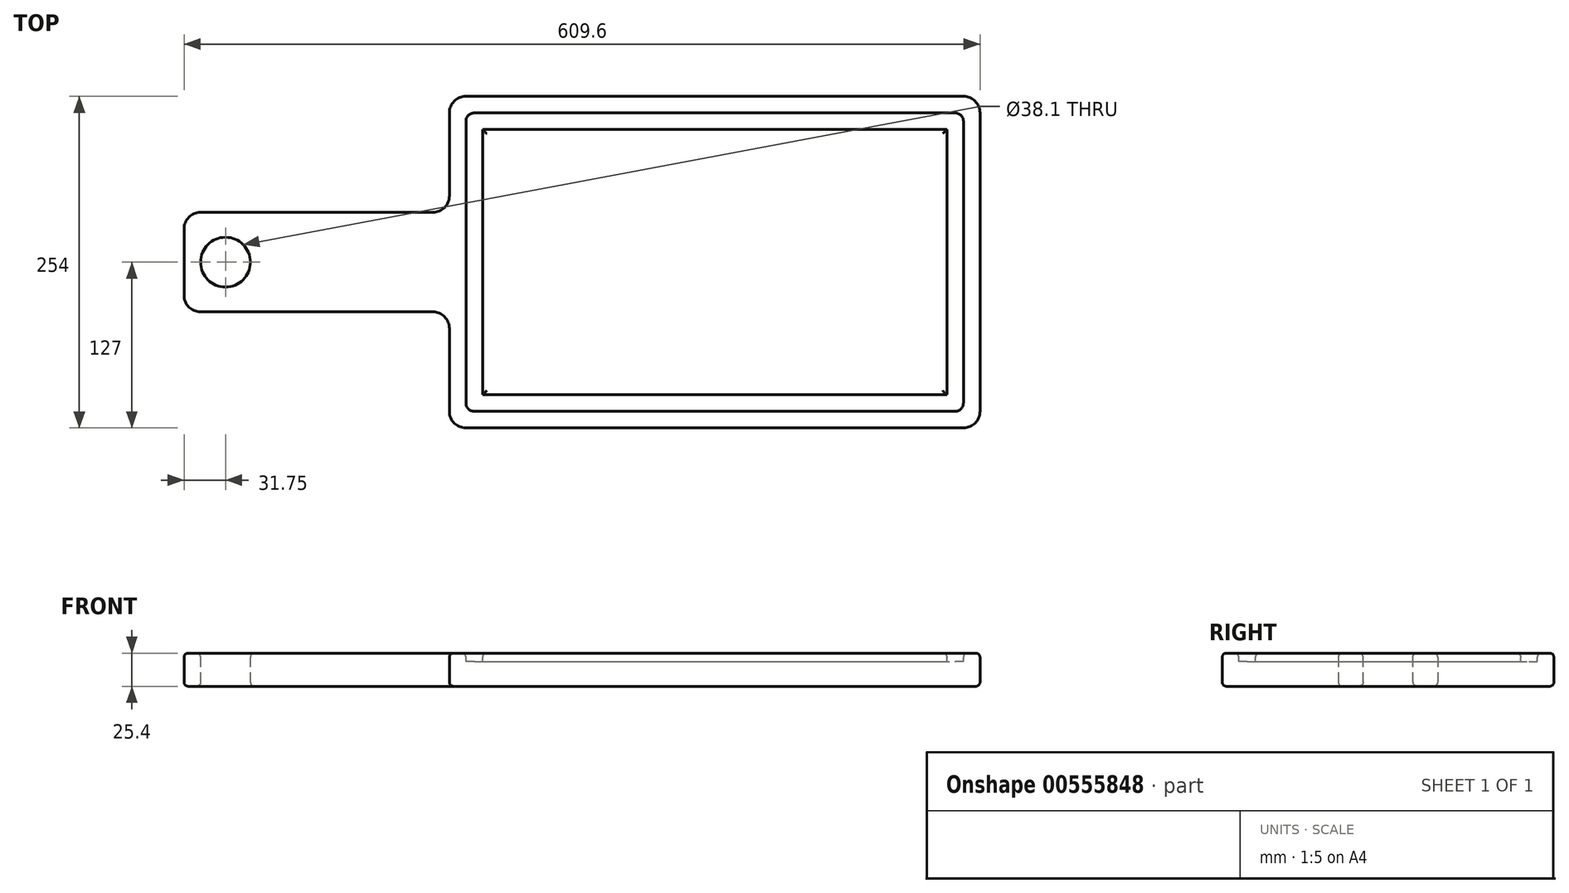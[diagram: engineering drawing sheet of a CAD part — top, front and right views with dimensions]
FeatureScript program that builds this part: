
annotation { "Feature Type Name" : "Feature", "Feature Type Description" : "" }
export const myFeature = defineFeature(function(context is Context, id is Id, definition is map)
    precondition{}
    {
        {
            var Q0;
            Q0=qCreatedBy(makeId("Top.planeOp"),FACE);
            var sketch = newSketch(context, id + "F0", { "sketchPlane" : qUnion([Q0])});
            skLineSegment(sketch, "E0.bottom", {"start": v(0, 0) * mm, "end": v(406.4, 0) * mm});
            skLineSegment(sketch, "E0.top", {"start": v(0, 254) * mm, "end": v(406.4, 254) * mm});
            skLineSegment(sketch, "E0.left", {"start": v(0, 0) * mm, "end": v(0, 254) * mm});
            skLineSegment(sketch, "E0.right", {"start": v(406.4, 0) * mm, "end": v(406.4, 254) * mm});
            skLineSegment(sketch, "E1.bottom", {"start": v(0, 165.1) * mm, "end": v(-203.2, 165.1) * mm});
            skLineSegment(sketch, "E1.top", {"start": v(0, 88.9) * mm, "end": v(-203.2, 88.9) * mm});
            skLineSegment(sketch, "E1.left", {"start": v(0, 165.1) * mm, "end": v(0, 88.9) * mm});
            skLineSegment(sketch, "E1.right", {"start": v(-203.2, 165.1) * mm, "end": v(-203.2, 88.9) * mm});
            skSolve(sketch);
        }
        {
            var Q0;
            {var subQ3=sQuery(id+"F0.wireOp",EDGE,"E0.bottom");Q0=makeQuery(id+"F0.imprint","IMPRINT",FACE,{"disambiguationData":[TD([[makeQuery(id+"F0.imprint","IMPRINT",EDGE,{"derivedFrom":subQ3}),1.0]])]});}
            var Q1;
            Q1=makeQuery(id+"F0.imprint","IMPRINT",FACE,{"disambiguationData":[TD([[makeQuery(id+"F0.imprint","IMPRINT",EDGE,{"derivedFrom":sQuery(id+"F0.wireOp",EDGE,"E1.bottom")}),1.0]])]});
            extrude(context, id + "F1", {"entities" : qUnion([Q0, Q1]), "depth" : 25.4 * mm, "offsetDistance" : 25.4 * mm});
        }
        {
            var Q0;
            Q0=makeQuery(id+"F1.opExtrude","CAP_FACE",FACE,{"disambiguationData":[OSD([sQuery(id+"F0.wireOp",EDGE,"E0.bottom"),sQuery(id+"F0.wireOp",EDGE,"E0.top"),sQuery(id+"F0.wireOp",EDGE,"E0.left"),sQuery(id+"F0.wireOp",EDGE,"E0.right"),sQuery(id+"F0.wireOp",EDGE,"E1.bottom"),sQuery(id+"F0.wireOp",EDGE,"E1.top"),sQuery(id+"F0.wireOp",EDGE,"E1.right")])],"isStart":false});
            var sketch = newSketch(context, id + "F2", { "sketchPlane" : qUnion([Q0])});
            skCircle(sketch, "E2", {"center": v(-171.45, 127) * mm, "radius": 19.05 * mm});
            skSolve(sketch);
        }
        {
            var Q0;
            Q0 = qSketchRegion(id + "F2", true);
            extrude(context, id + "F3", {"entities" : qUnion([Q0]), "operationType" : NewBodyOperationType.REMOVE, "oppositeDirection" : true, "depth" : 25.4 * mm, "offsetDistance" : 25.4 * mm});
        }
        {
            var Q0;
            Q0=makeQuery(id+"F1.opExtrude","CAP_FACE",FACE,{"disambiguationData":[OSD([sQuery(id+"F0.wireOp",EDGE,"E0.bottom"),sQuery(id+"F0.wireOp",EDGE,"E0.top"),sQuery(id+"F0.wireOp",EDGE,"E0.left"),sQuery(id+"F0.wireOp",EDGE,"E0.right"),sQuery(id+"F0.wireOp",EDGE,"E1.bottom"),sQuery(id+"F0.wireOp",EDGE,"E1.top"),sQuery(id+"F0.wireOp",EDGE,"E1.right")])],"isStart":false});
            var sketch = newSketch(context, id + "F4", { "sketchPlane" : qUnion([Q0])});
            skLineSegment(sketch, "E3.0", {"start": v(12.7, 12.7) * mm, "end": v(12.7, 88.9) * mm});
            skLineSegment(sketch, "E3.1", {"start": v(12.7, 165.1) * mm, "end": v(12.7, 241.3) * mm});
            skLineSegment(sketch, "E3.2", {"start": v(12.7, 241.3) * mm, "end": v(393.7, 241.3) * mm});
            skLineSegment(sketch, "E3.3", {"start": v(393.7, 12.7) * mm, "end": v(393.7, 241.3) * mm});
            skLineSegment(sketch, "E3.4", {"start": v(12.7, 12.7) * mm, "end": v(393.7, 12.7) * mm});
            skLineSegment(sketch, "E4", {"start": v(12.7, 165.1) * mm, "end": v(12.7, 88.9) * mm});
            skLineSegment(sketch, "E5.0", {"start": v(25.4, 165.1) * mm, "end": v(25.4, 228.6) * mm});
            skLineSegment(sketch, "E5.1", {"start": v(381, 25.4) * mm, "end": v(381, 228.6) * mm});
            skLineSegment(sketch, "E5.2", {"start": v(25.4, 25.4) * mm, "end": v(381, 25.4) * mm});
            skLineSegment(sketch, "E5.3", {"start": v(25.4, 228.6) * mm, "end": v(381, 228.6) * mm});
            skLineSegment(sketch, "E5.4", {"start": v(25.4, 25.4) * mm, "end": v(25.4, 88.9) * mm});
            skLineSegment(sketch, "E5.5", {"start": v(25.4, 165.1) * mm, "end": v(25.4, 88.9) * mm});
            skSolve(sketch);
        }
        {
            var Q0;
            Q0=makeQuery(id+"F4.imprint","IMPRINT",FACE,{"disambiguationData":[TD([[makeQuery(id+"F4.imprint","IMPRINT",EDGE,{"derivedFrom":sQuery(id+"F4.wireOp",EDGE,"E3.0")}),-1.0]])]});
            extrude(context, id + "F5", {"entities" : qUnion([Q0]), "operationType" : NewBodyOperationType.REMOVE, "oppositeDirection" : true, "depth" : 6.35 * mm, "offsetDistance" : 25.4 * mm});
        }
        {
            var Q0;
            Q0=makeQuery(id+"F5.boolean.opBoolean","COPY",EDGE,{"derivedFrom":makeQuery(id+"F5.opExtrude","SWEPT_EDGE",EDGE,{"disambiguationData":[OSD([sQuery(id+"F4.wireOp",EDGE,"E3.1"),sQuery(id+"F4.wireOp",EDGE,"E3.2")])]})});
            var Q1;
            Q1=makeQuery(id+"F5.boolean.opBoolean","COPY",EDGE,{"derivedFrom":makeQuery(id+"F5.opExtrude","SWEPT_EDGE",EDGE,{"disambiguationData":[OSD([sQuery(id+"F4.wireOp",EDGE,"E3.3"),sQuery(id+"F4.wireOp",EDGE,"E3.4")])]})});
            var Q2;
            Q2=makeQuery(id+"F5.boolean.opBoolean","COPY",EDGE,{"derivedFrom":makeQuery(id+"F5.opExtrude","SWEPT_EDGE",EDGE,{"disambiguationData":[OSD([sQuery(id+"F4.wireOp",EDGE,"E3.0"),sQuery(id+"F4.wireOp",EDGE,"E3.4")])]})});
            var Q3;
            Q3=makeQuery(id+"F5.boolean.opBoolean","COPY",EDGE,{"derivedFrom":makeQuery(id+"F5.opExtrude","SWEPT_EDGE",EDGE,{"disambiguationData":[OSD([sQuery(id+"F4.wireOp",EDGE,"E3.2"),sQuery(id+"F4.wireOp",EDGE,"E3.3")])]})});
            fillet(context, id + "F6", {"entities" : qUnion([Q0, Q1, Q2, Q3]), "radius" : 6.35 * mm, "tangentPropagation" : true, "allowEdgeOverflow" : false});
        }
        {
            var Q0;
            Q0=makeQuery(id+"F1.opExtrude","SWEPT_EDGE",EDGE,{"disambiguationData":[OSD([sQuery(id+"F0.wireOp",EDGE,"E0.bottom"),sQuery(id+"F0.wireOp",EDGE,"E0.right")])]});
            var Q1;
            Q1=makeQuery(id+"F1.opExtrude","SWEPT_EDGE",EDGE,{"disambiguationData":[OSD([sQuery(id+"F0.wireOp",EDGE,"E0.bottom"),sQuery(id+"F0.wireOp",EDGE,"E0.left")])]});
            var Q2;
            Q2=makeQuery(id+"F1.opExtrude","SWEPT_EDGE",EDGE,{"disambiguationData":[OSD([sQuery(id+"F0.wireOp",EDGE,"E0.left"),sQuery(id+"F0.wireOp",EDGE,"E1.top"),sQuery(id+"F0.wireOp",EDGE,"E1.left")])]});
            var Q3;
            Q3=makeQuery(id+"F1.opExtrude","SWEPT_EDGE",EDGE,{"disambiguationData":[OSD([sQuery(id+"F0.wireOp",EDGE,"E1.top"),sQuery(id+"F0.wireOp",EDGE,"E1.right")])]});
            var Q4;
            Q4=makeQuery(id+"F1.opExtrude","SWEPT_EDGE",EDGE,{"disambiguationData":[OSD([sQuery(id+"F0.wireOp",EDGE,"E1.bottom"),sQuery(id+"F0.wireOp",EDGE,"E1.right")])]});
            var Q5;
            Q5=makeQuery(id+"F1.opExtrude","SWEPT_EDGE",EDGE,{"disambiguationData":[OSD([sQuery(id+"F0.wireOp",EDGE,"E0.left"),sQuery(id+"F0.wireOp",EDGE,"E1.bottom"),sQuery(id+"F0.wireOp",EDGE,"E1.left")])]});
            var Q6;
            Q6=makeQuery(id+"F1.opExtrude","SWEPT_EDGE",EDGE,{"disambiguationData":[OSD([sQuery(id+"F0.wireOp",EDGE,"E0.top"),sQuery(id+"F0.wireOp",EDGE,"E0.left")])]});
            var Q7;
            Q7=makeQuery(id+"F1.opExtrude","SWEPT_EDGE",EDGE,{"disambiguationData":[OSD([sQuery(id+"F0.wireOp",EDGE,"E0.top"),sQuery(id+"F0.wireOp",EDGE,"E0.right")])]});
            fillet(context, id + "F7", {"entities" : qUnion([Q0, Q1, Q2, Q3, Q4, Q5, Q6, Q7]), "radius" : 12.7 * mm, "tangentPropagation" : true, "allowEdgeOverflow" : false});
        }
        {
            var Q0;
            Q0=makeQuery(id+"F5.boolean.opBoolean","SPLIT",FACE,{"disambiguationData":[TD([makeQuery(id+"F5.opExtrude","SWEPT_FACE",FACE,{"disambiguationData":[OSD([sQuery(id+"F4.wireOp",EDGE,"E5.1")])]})])],"derivedFrom":makeQuery(id+"F1.opExtrude","CAP_FACE",FACE,{"disambiguationData":[OSD([sQuery(id+"F0.wireOp",EDGE,"E0.bottom"),sQuery(id+"F0.wireOp",EDGE,"E0.top"),sQuery(id+"F0.wireOp",EDGE,"E0.left"),sQuery(id+"F0.wireOp",EDGE,"E0.right"),sQuery(id+"F0.wireOp",EDGE,"E1.bottom"),sQuery(id+"F0.wireOp",EDGE,"E1.top"),sQuery(id+"F0.wireOp",EDGE,"E1.right")])],"isStart":false})});
            var Q1;
            {var subQ0=sQuery(id+"F0.wireOp",EDGE,"E1.right");var subQ1=sQuery(id+"F0.wireOp",EDGE,"E1.top");var subQ2=sQuery(id+"F0.wireOp",EDGE,"E1.bottom");var subQ3=sQuery(id+"F0.wireOp",EDGE,"E0.right");var subQ4=sQuery(id+"F0.wireOp",EDGE,"E0.bottom");var subQ5=sQuery(id+"F0.wireOp",EDGE,"E0.left");var subQ6=sQuery(id+"F0.wireOp",EDGE,"E0.top");Q1=makeQuery(id+"F5.boolean.opBoolean","SPLIT",FACE,{"disambiguationData":[TD([makeQuery(id+"F1.opExtrude","SWEPT_FACE",FACE,{"disambiguationData":[OSD([subQ4])]})])],"derivedFrom":makeQuery(id+"F1.opExtrude","CAP_FACE",FACE,{"disambiguationData":[OSD([subQ4,subQ6,subQ5,subQ3,subQ2,subQ1,subQ0])],"isStart":false})});}
            var Q2;
            Q2=makeQuery(id+"F1.opExtrude","CAP_FACE",FACE,{"disambiguationData":[OSD([sQuery(id+"F0.wireOp",EDGE,"E0.bottom"),sQuery(id+"F0.wireOp",EDGE,"E0.top"),sQuery(id+"F0.wireOp",EDGE,"E0.left"),sQuery(id+"F0.wireOp",EDGE,"E0.right"),sQuery(id+"F0.wireOp",EDGE,"E1.bottom"),sQuery(id+"F0.wireOp",EDGE,"E1.top"),sQuery(id+"F0.wireOp",EDGE,"E1.right")])],"isStart":true});
            fillet(context, id + "F8", {"entities" : qUnion([Q0, Q1, Q2]), "radius" : 3.17 * mm, "tangentPropagation" : true, "allowEdgeOverflow" : false});
        }
    });
